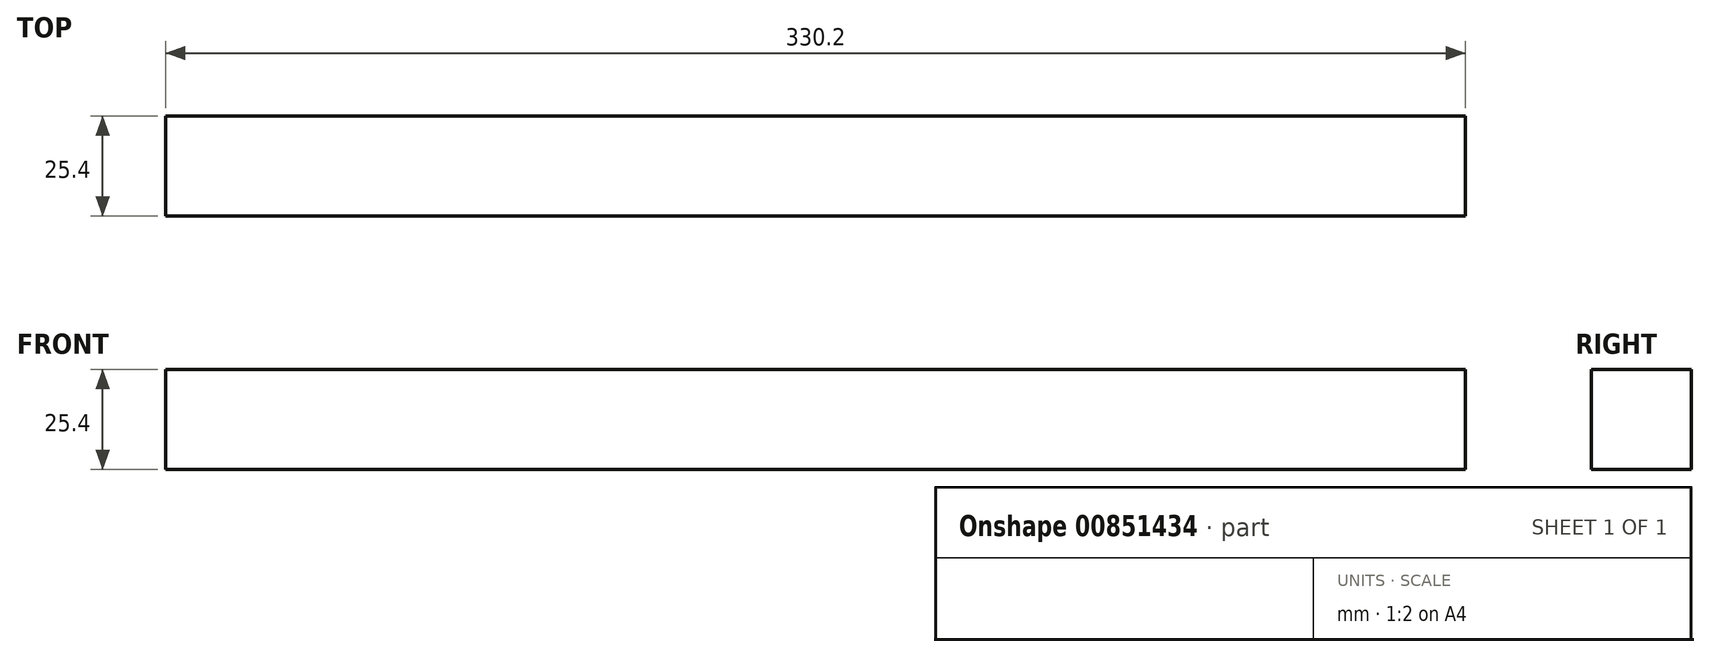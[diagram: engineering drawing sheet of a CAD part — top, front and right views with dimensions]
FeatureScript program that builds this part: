
annotation { "Feature Type Name" : "Feature", "Feature Type Description" : "" }
export const myFeature = defineFeature(function(context is Context, id is Id, definition is map)
    precondition{}
    {
        {
            var Q0;
            Q0=qCreatedBy(makeId("Front.planeOp"),FACE);
            var sketch = newSketch(context, id + "F0", { "sketchPlane" : qUnion([Q0])});
            skLineSegment(sketch, "E0.bottom", {"start": v(-148.57, -3.57) * mm, "end": v(181.63, -3.57) * mm});
            skLineSegment(sketch, "E0.top", {"start": v(-148.57, -28.97) * mm, "end": v(181.63, -28.97) * mm});
            skLineSegment(sketch, "E0.left", {"start": v(-148.57, -3.57) * mm, "end": v(-148.57, -28.97) * mm});
            skLineSegment(sketch, "E0.right", {"start": v(181.63, -3.57) * mm, "end": v(181.63, -28.97) * mm});
            skSolve(sketch);
        }
        {
            var Q0;
            Q0 = qSketchRegion(id + "F0", true);
            extrude(context, id + "F1", {"entities" : qUnion([Q0]), "depth" : 25.4 * mm, "offsetDistance" : 25.4 * mm});
        }
    });
